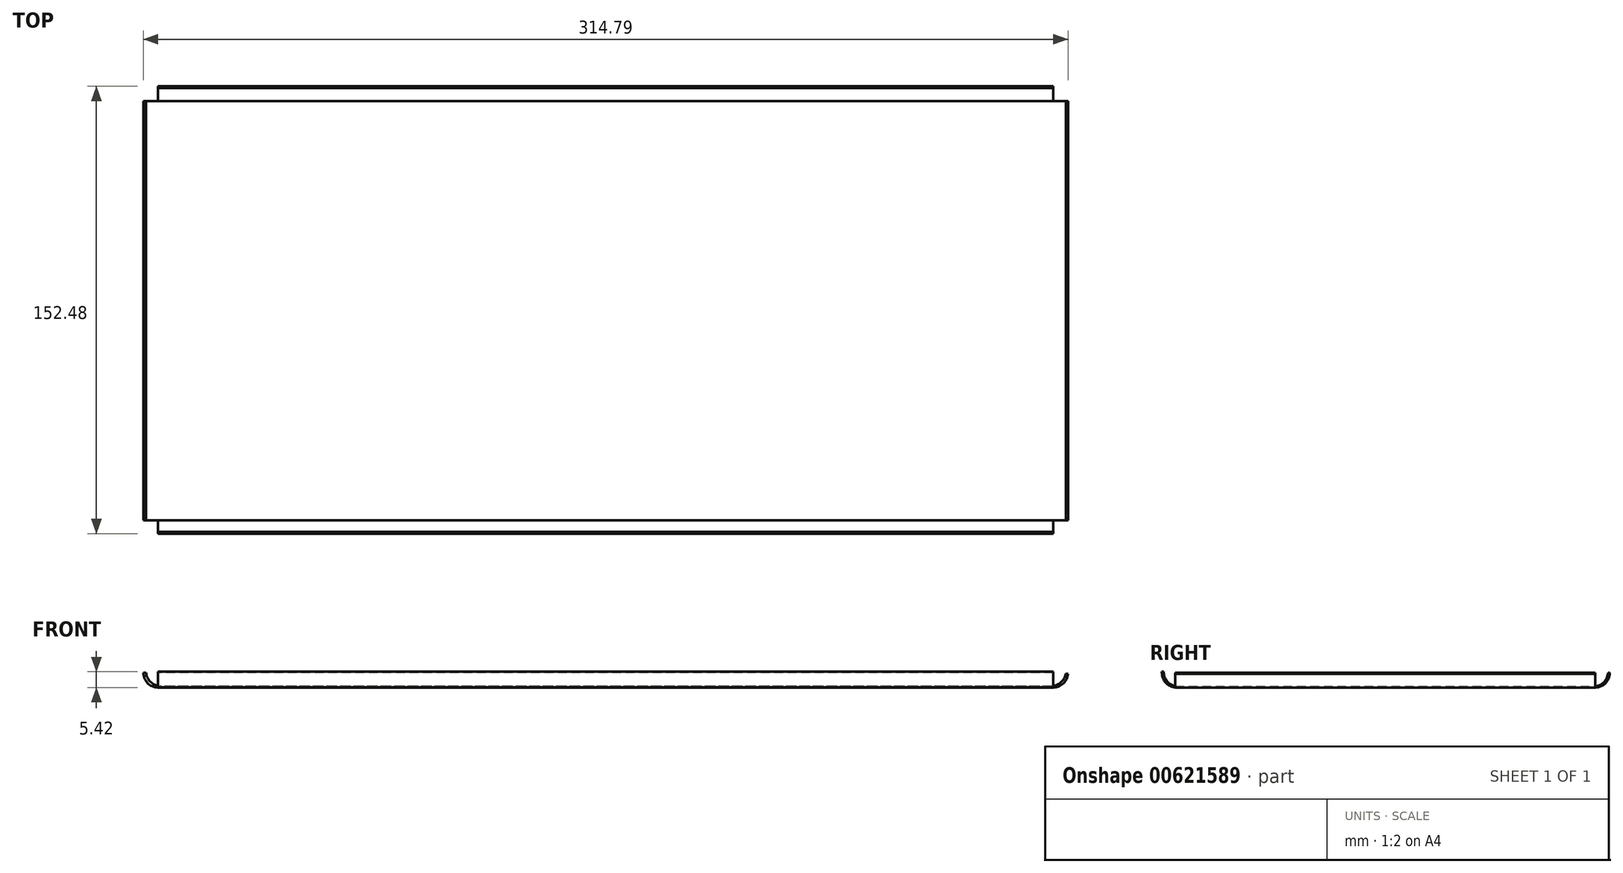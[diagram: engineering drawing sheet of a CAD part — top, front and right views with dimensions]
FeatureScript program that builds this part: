
annotation { "Feature Type Name" : "Feature", "Feature Type Description" : "" }
export const myFeature = defineFeature(function(context is Context, id is Id, definition is map)
    precondition{}
    {
        {
            var Q0;
            Q0=qCreatedBy(makeId("Right.planeOp"),FACE);
            var sketch = newSketch(context, id + "F0", { "sketchPlane" : qUnion([Q0])});
            skLineSegment(sketch, "E0.top", {"start": v(-71.5, 0) * mm, "end": v(70.99, 0) * mm});
            skLineSegment(sketch, "E0.left", {"start": v(-76.5, 5.42) * mm, "end": v(-76.5, 5) * mm});
            skLineSegment(sketch, "E0.right", {"start": v(75.99, 5) * mm, "end": v(75.99, 4.66) * mm});
            skPoint(sketch, "E1.visualSharp", {"position": v(-76.5, 0) * mm});
            skArc(sketch, "E1.filletArc", {"start": v(-76.5, 5) * mm, "mid": v(-75.03, 1.46) * mm, "end": v(-71.5, 0) * mm});
            skPoint(sketch, "E2.visualSharp", {"position": v(75.99, 0) * mm});
            skArc(sketch, "E2.filletArc", {"start": v(70.99, 0) * mm, "mid": v(74.53, 1.46) * mm, "end": v(75.99, 5) * mm});
            skLineSegment(sketch, "E3.top", {"start": v(-70.9, 0.35) * mm, "end": v(70.42, 0.35) * mm});
            skArc(sketch, "E4.filletArc", {"start": v(-75.9, 5.39) * mm, "mid": v(-74.44, 1.83) * mm, "end": v(-70.9, 0.35) * mm});
            skArc(sketch, "E5.filletArc", {"start": v(70.42, 0.35) * mm, "mid": v(73.83, 1.7) * mm, "end": v(75.41, 5) * mm});
            skLineSegment(sketch, "E6", {"start": v(-76.5, 5.42) * mm, "end": v(-75.9, 5.39) * mm});
            skLineSegment(sketch, "E7", {"start": v(75.41, 5) * mm, "end": v(75.99, 5) * mm});
            skLineSegment(sketch, "E8", {"start": v(75.99, 5) * mm, "end": v(75.99, 0) * mm});
            skLineSegment(sketch, "E9", {"start": v(70.99, 0) * mm, "end": v(70.99, 5) * mm});
            skSolve(sketch);
        }
        {
            var Q0;
            Q0=makeQuery(id+"F0.imprint","IMPRINT",FACE,{"disambiguationData":[TD([[makeQuery(id+"F0.imprint","IMPRINT",EDGE,{"derivedFrom":sQuery(id+"F0.wireOp",EDGE,"E0.top")}),1.0]])]});
            var Q1;
            {var subQ0=sQuery(id+"F0.wireOp",EDGE,"E2.filletArc");Q1=makeQuery(id+"F0.imprint","IMPRINT",FACE,{"disambiguationData":[TD([[makeQuery(id+"F0.imprint","IMPRINT",EDGE,{"derivedFrom":subQ0}),1.0]])]});}
            extrude(context, id + "F1", {"entities" : qUnion([Q0, Q1]), "depth" : 304.8 * mm, "offsetDistance" : 30.48 * mm});
        }
        {
            var Q0;
            Q0=qCreatedBy(makeId("Front.planeOp"),FACE);
            var Q1;
            Q1=sQuery(id+"F0.wireOp",EDGE,"E9");
            cPlane(context, id + "F2", {"entities" : qUnion([Q0, Q1]), "cplaneType" : CPlaneType.LINE_ANGLE, "offset" : 25.4 * mm, "angle" : 0 * degree, "width" : 152.4 * mm, "height" : 152.4 * mm});
        }
        {
            var Q0;
            Q0=qCreatedBy(id+"F2.planeOp",FACE);
            var sketch = newSketch(context, id + "F3", { "sketchPlane" : qUnion([Q0])});
            skLineSegment(sketch, "E10.top", {"start": v(-304.8, 0) * mm, "end": v(0, 0) * mm});
            skArc(sketch, "E11.filletArc", {"start": v(-309.8, 4.7) * mm, "mid": v(-308.23, 1.36) * mm, "end": v(-304.8, 0) * mm});
            skArc(sketch, "E12.filletArc", {"start": v(0, 0) * mm, "mid": v(3.54, 1.46) * mm, "end": v(5, 5) * mm});
            skPoint(sketch, "E13.0", {"position": v(-304.8, 0) * mm});
            skPoint(sketch, "E14.0", {"position": v(0, 0) * mm});
            skLineSegment(sketch, "E15.top", {"start": v(-304.11, 0.51) * mm, "end": v(-0.9, 0.51) * mm});
            skArc(sketch, "E16.filletArc", {"start": v(-309.05, 4.72) * mm, "mid": v(-307.36, 1.7) * mm, "end": v(-304.11, 0.51) * mm});
            skArc(sketch, "E17.filletArc", {"start": v(-0.9, 0.51) * mm, "mid": v(2.44, 1.8) * mm, "end": v(4.06, 5) * mm});
            skLineSegment(sketch, "E18", {"start": v(4.06, 5) * mm, "end": v(5, 5) * mm});
            skLineSegment(sketch, "E19", {"start": v(-309.05, 4.72) * mm, "end": v(-309.8, 4.7) * mm});
            skSolve(sketch);
        }
        {
            var Q0;
            Q0=makeQuery(id+"F3.imprint","IMPRINT",FACE,{"disambiguationData":[TD([[makeQuery(id+"F3.imprint","IMPRINT",EDGE,{"derivedFrom":sQuery(id+"F3.wireOp",EDGE,"E10.top")}),1.0]])]});
            extrude(context, id + "F4", {"entities" : qUnion([Q0]), "operationType" : NewBodyOperationType.ADD, "oppositeDirection" : true, "depth" : 142.95 * mm, "offsetDistance" : 30.48 * mm});
        }
    });
